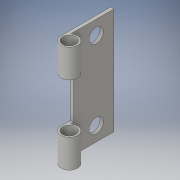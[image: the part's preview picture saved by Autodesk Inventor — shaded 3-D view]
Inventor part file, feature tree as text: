
AUTODESK INVENTOR PART (.ipt)
format: ipt  version: 2016 (Build 200138000, 138)  size: 136,704 bytes
history: native  units: in
note: dims shown in document units (in); Inventor stores cm internally (conversion verified against a paired STEP export)
features: extrude x3, sketch x3, plane x1, projected_geometry x1
ambient origin geometry x8: Origin, YZ Plane, XZ Plane, XY Plane, X Axis, Y Axis, Z Axis, Center Point
bodies: Solid1 (feature_tree)
feature tree (8):
  extrude  "Extrusion1"  Depth=0.233in
  plane  "Work Plane1"
  extrude  "Extrusion2"  Depth=0.045in
  extrude  "Extrusion3"  Depth=0.4in
  sketch  "Sketch1"  dims[d0=0.188in d1=0.233in]
  sketch  "Sketch2"  dims[d2=0.7in d3=0.045in]
  projected_geometry  "Projected Loop1"
  sketch  "Sketch3"  dims[d4=1.5in d5=0.0in d6=0.4in d7=0.0in d8=0.2402in d9=0.8364in d10=0.5686in d11=0.7in d12=0.0in d13=0.25in d14=0.2in d15=0.2in d17=0.2in d18=0.7in d19=0.0in]
